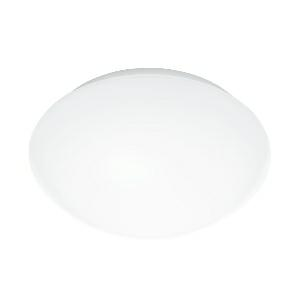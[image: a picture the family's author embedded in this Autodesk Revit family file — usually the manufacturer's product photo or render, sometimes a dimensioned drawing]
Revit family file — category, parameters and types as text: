
# Revit family: rs_pro_led_p1_sl_056049
name_source: partatom
category: Leuchten
revit_build: Autodesk Revit 2016 (Build: 20190508_0715(x64)
units: mm (PartAtom-declared; Revit-internal decimal feet)

## family parameters
Basisbauteil = Fläche
Beim Laden mit Abzugskörper schneiden = Nein
Bemaßung runder Anschluss = Durchmesser verwenden
Gemeinsam genutzt = Nein
Lichtquelle = Nein
Raumberechnungspunkt = Nein
Teiletyp = Normal

## types (1)
- RS PRO LED P1 SL (1 x , 1010 lm, 4000 K)
    Beschreibung = Dimensions (Ø x H): 280 x 110 mm; Mains power supply: 220 – 240 V / 50 – 60 Hz; Output: 9 W; Luminous flux: 1010 lm; Colour temperature: 4000 K; Colour variation LED: SDCM3; Colour Rendering Index CRI: 80-89; With lamp: Yes, STEINEL LED system; Lamp: LED cannot be replaced; LED life expectancy (max. °C): 50000 h; Drop in luminous flux in accordance with LM80: L80B10; Base: without; LED cooling system: Passive Thermo Control; With motion detector: No; Photo-cell controller: No; Basic light level function: No; Soft light start: Yes; Impact resistance: IK03; IP-rating: IP54; Protection class: II; Ambient temperature: 10 – 40 °C; Housing material: Plastic; Cover material: Plastic, opal; Manufacturer's Warranty: 5 years; With remote control: No; Version: Neutral white; PU1, EAN: 4007841056049
    CIE Flux Codes = 41 70 89 89 100
    Color Rendering = 80-89
    Color Temperature = 4000 K
    Frequency = 50 Hz, 60 Hz
    Height = 0 mm  [stored 0 ft]
    Hersteller = Steinel
    Lamp Light Flux = 1010 lm
    Lamp count = 1
    Lampe = 1 x
    Length = 280 mm
    Luminous efficacy = 112 lm/W
    ModVariant = Nein
    Modell = 056049
    Mounting Type = Surface mounted
    Number of Poles = 1
    OnlyDefault = Ja
    Power Factor = 1
    Product Name = RS PRO LED P1 SL
    Product group = Sensor-switched indoor light
    ProductGroupID = 30
    Protection Class = Protection class II
    Protection Degree = IP 54
    RlxData = <blob elided: 60813 chars, md5=e59c090d>
    Scheinlast = 9 VA
    Socket = socket
    Standby Power = 0 W
    System Light Flux = 1010 lm
    System Power = 9 W
    Typenbild = produkt1_056049.jpg
    Typenkommentare = Product without accessories
    URL = http://relux.com
    VarID = ---
    Voltage = 0 V
    Vorgabe-Ansicht = 1800 mm
    Weight = 0.00 kg
    Width = 0 mm  [stored 0 ft]

note: [stored X ft] marks values corroborated as IEEE doubles in the binary element streams (Revit-internal decimal feet)

## geometry (parser evidence)
native form markers: Blend x4, Sweep x16
no freeform markers — native parametric forms only
